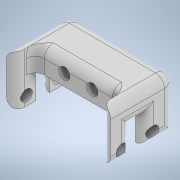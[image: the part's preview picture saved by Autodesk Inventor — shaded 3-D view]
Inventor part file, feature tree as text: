
AUTODESK INVENTOR PART (.ipt)
format: ipt  version: 2022 (Build 260153000, 153)  size: 248,832 bytes
history: native  units: in
note: dims shown in document units (in); Inventor stores cm internally (conversion verified against a paired STEP export)
features: extrude x3, sketch x3, fillet x2, projected_geometry x2
ambient origin geometry x8: Origin, YZ Plane, XZ Plane, XY Plane, X Axis, Y Axis, Z Axis, Center Point
bodies: Solid1 (feature_tree)
feature tree (10):
  extrude  "Extrusion1"  Depth=0.125in
  extrude  "Extrusion2"  Depth=0.325in
  extrude  "Extrusion3"  Depth=0.125in
  fillet  "Fillet1"  Radius=0.157in
  fillet  "Fillet2"  Radius=0.6in
  sketch  "Sketch1"  dims[d0=0.375in d1=0.125in]
  sketch  "Sketch2"  dims[d2=1.45in d3=0.325in]
  projected_geometry  "Projected Loop1"
  sketch  "Sketch3"  dims[d4=0.157in d5=0.195in d6=0.157in d7=0.6in d8=0.0in d9=0.4in d10=0.0in d11=0.25in d13=0.157in d14=0.043in d15=0.0in d16=0.0in d17=0.125in d18=0.125in]
  projected_geometry  "Projected Loop2"
